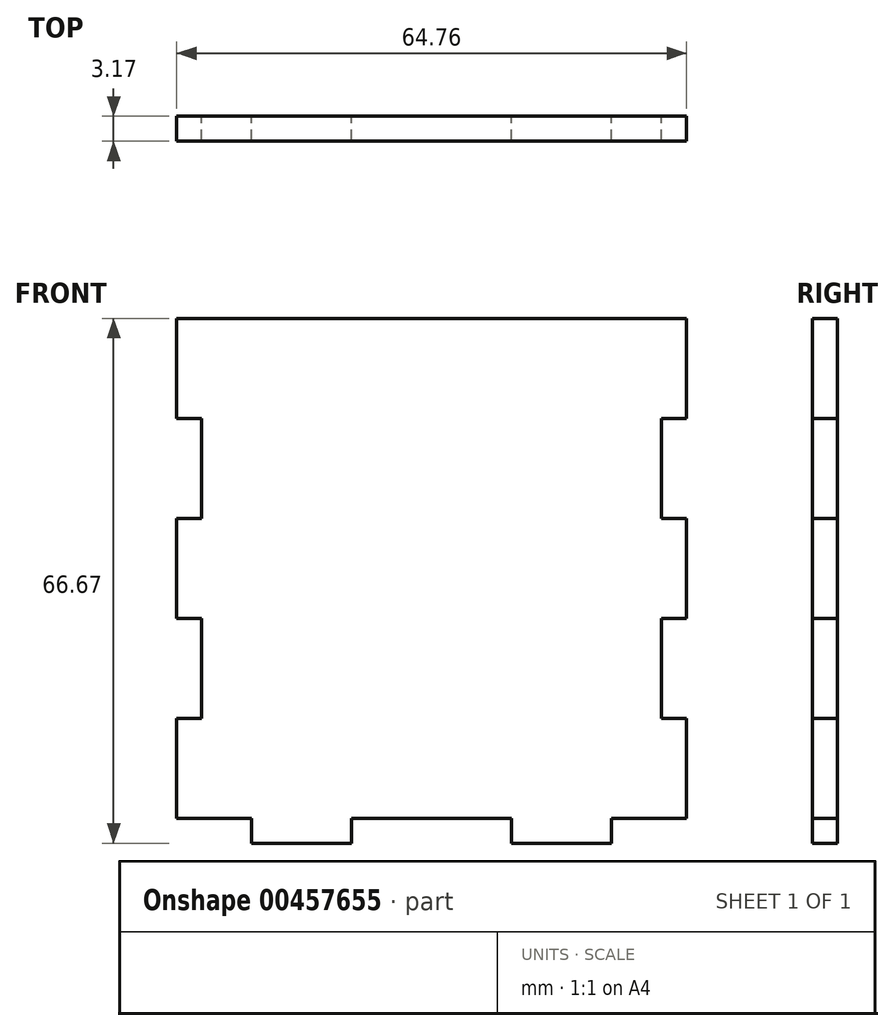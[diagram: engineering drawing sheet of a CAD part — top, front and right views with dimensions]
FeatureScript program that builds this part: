
annotation { "Feature Type Name" : "Feature", "Feature Type Description" : "" }
export const myFeature = defineFeature(function(context is Context, id is Id, definition is map)
    precondition{}
    {
        {
            var Q0;
            Q0=qCreatedBy(makeId("Front.planeOp"),FACE);
            var sketch = newSketch(context, id + "F0", { "sketchPlane" : qUnion([Q0])});
            skLineSegment(sketch, "E0.bottom", {"start": v(32.39, -31.75) * mm, "end": v(22.86, -31.75) * mm});
            skLineSegment(sketch, "E0.top", {"start": v(32.39, 31.75) * mm, "end": v(-32.39, 31.75) * mm});
            skLineSegment(sketch, "E0.left", {"start": v(32.39, -31.75) * mm, "end": v(32.39, -19.05) * mm});
            skLineSegment(sketch, "E0.right", {"start": v(-32.39, -31.75) * mm, "end": v(-32.39, -19.05) * mm});
            skPoint(sketch, "E0.middle", {"position": v(0, 0) * mm});
            skLineSegment(sketch, "E1.bottom", {"start": v(-22.86, -34.93) * mm, "end": v(-10.16, -34.93) * mm});
            skLineSegment(sketch, "E1.left", {"start": v(-22.86, -31.75) * mm, "end": v(-22.86, -34.93) * mm});
            skLineSegment(sketch, "E1.right", {"start": v(-10.16, -31.75) * mm, "end": v(-10.16, -34.93) * mm});
            skLineSegment(sketch, "E2.top", {"start": v(10.16, -34.93) * mm, "end": v(22.86, -34.93) * mm});
            skLineSegment(sketch, "E2.left", {"start": v(10.16, -31.75) * mm, "end": v(10.16, -34.93) * mm});
            skLineSegment(sketch, "E2.right", {"start": v(22.86, -31.75) * mm, "end": v(22.86, -34.93) * mm});
            skLineSegment(sketch, "E3.trimOffspring", {"start": v(-22.86, -31.75) * mm, "end": v(-32.39, -31.75) * mm});
            skLineSegment(sketch, "E4.trimOffspring", {"start": v(10.16, -31.75) * mm, "end": v(-10.16, -31.75) * mm});
            skLineSegment(sketch, "E5.bottom", {"start": v(-32.39, 19.05) * mm, "end": v(-29.21, 19.05) * mm});
            skLineSegment(sketch, "E5.top", {"start": v(-32.39, 6.35) * mm, "end": v(-29.21, 6.35) * mm});
            skLineSegment(sketch, "E5.right", {"start": v(-29.21, 19.05) * mm, "end": v(-29.21, 6.35) * mm});
            skLineSegment(sketch, "E6.bottom", {"start": v(-32.39, -6.35) * mm, "end": v(-29.21, -6.35) * mm});
            skLineSegment(sketch, "E6.top", {"start": v(-32.39, -19.05) * mm, "end": v(-29.21, -19.05) * mm});
            skLineSegment(sketch, "E6.right", {"start": v(-29.21, -6.35) * mm, "end": v(-29.21, -19.05) * mm});
            skLineSegment(sketch, "E7.bottom", {"start": v(32.39, 19.05) * mm, "end": v(29.21, 19.05) * mm});
            skLineSegment(sketch, "E7.top", {"start": v(32.39, 6.35) * mm, "end": v(29.21, 6.35) * mm});
            skLineSegment(sketch, "E7.right", {"start": v(29.21, 19.05) * mm, "end": v(29.21, 6.35) * mm});
            skLineSegment(sketch, "E8.bottom", {"start": v(32.39, -6.35) * mm, "end": v(29.21, -6.35) * mm});
            skLineSegment(sketch, "E8.top", {"start": v(32.39, -19.05) * mm, "end": v(29.21, -19.05) * mm});
            skLineSegment(sketch, "E8.right", {"start": v(29.21, -6.35) * mm, "end": v(29.21, -19.05) * mm});
            skLineSegment(sketch, "E9.trimOffspring", {"start": v(-32.39, 19.05) * mm, "end": v(-32.39, 31.75) * mm});
            skLineSegment(sketch, "E10.trimOffspring", {"start": v(-32.39, -6.35) * mm, "end": v(-32.39, 6.35) * mm});
            skLineSegment(sketch, "E11.trimOffspring", {"start": v(32.39, -6.35) * mm, "end": v(32.39, 6.35) * mm});
            skLineSegment(sketch, "E12.trimOffspring", {"start": v(32.39, 19.05) * mm, "end": v(32.39, 31.75) * mm});
            skSolve(sketch);
        }
        {
            var Q0;
            Q0 = qSketchRegion(id + "F0", true);
            extrude(context, id + "F1", {"entities" : qUnion([Q0]), "depth" : 3.17 * mm});
        }
    });
